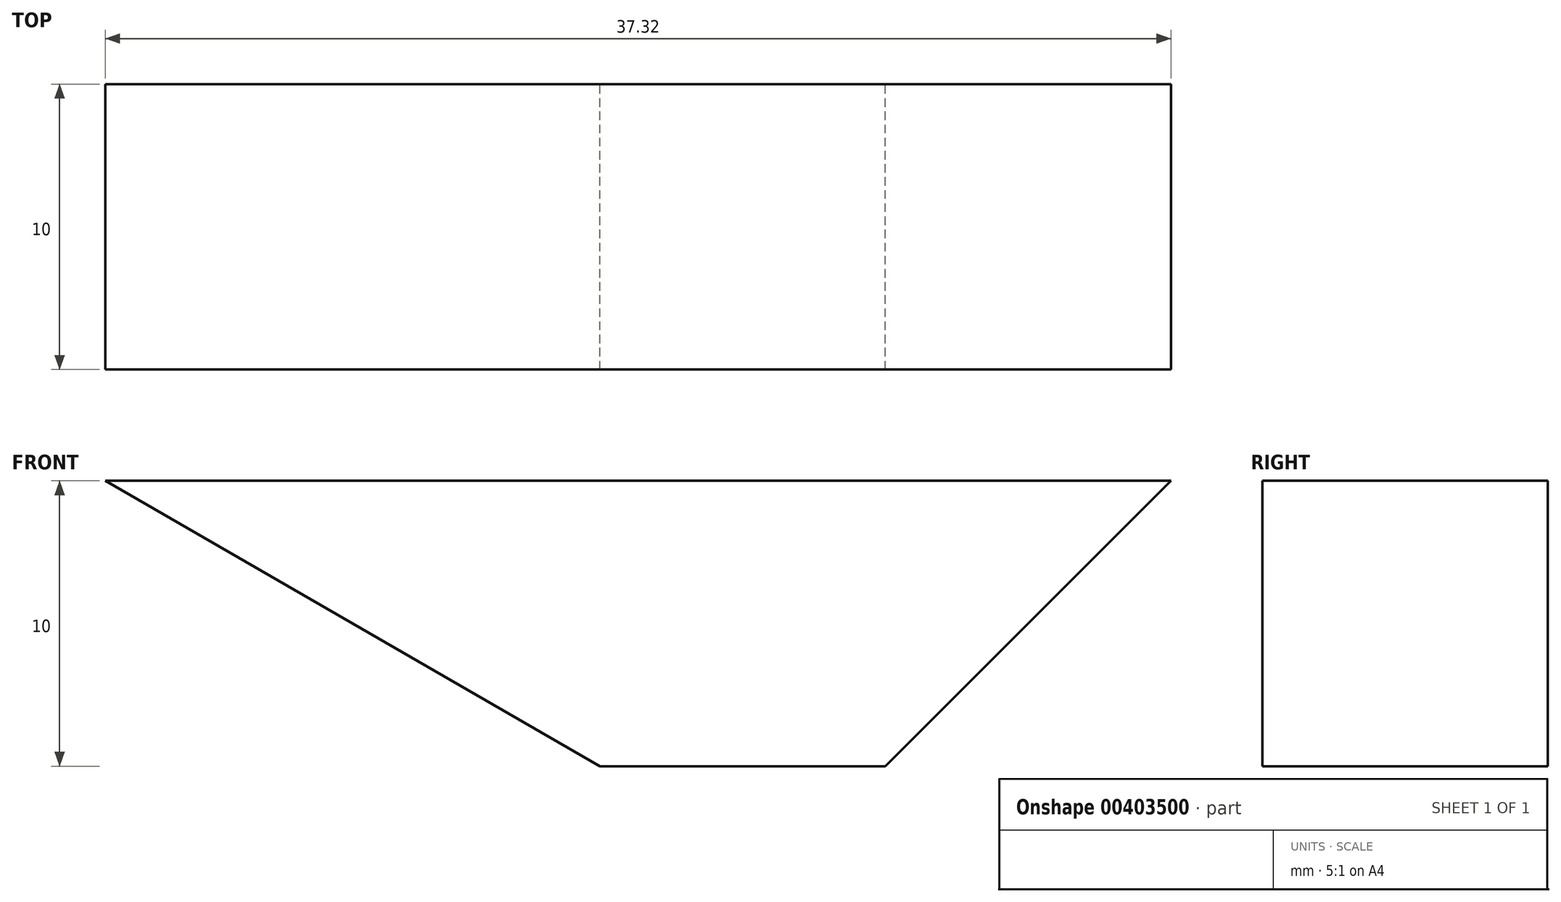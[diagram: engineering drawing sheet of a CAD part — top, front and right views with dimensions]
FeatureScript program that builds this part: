
annotation { "Feature Type Name" : "Feature", "Feature Type Description" : "" }
export const myFeature = defineFeature(function(context is Context, id is Id, definition is map)
    precondition{}
    {
        {
            var Q0;
            Q0=qCreatedBy(makeId("Front.planeOp"),FACE);
            var sketch = newSketch(context, id + "F0", { "sketchPlane" : qUnion([Q0]) });
            skLineSegment(sketch, "E0", {"start": v(0, 0) * mm, "end": v(-17.32, 10) * mm});
            skLineSegment(sketch, "E1", {"start": v(-17.32, 10) * mm, "end": v(20, 10) * mm});
            skLineSegment(sketch, "E2", {"start": v(20, 10) * mm, "end": v(10, 0) * mm});
            skLineSegment(sketch, "E3", {"start": v(10, 0) * mm, "end": v(0, 0) * mm});
            skSolve(sketch);
        }
        {
            var Q0;
            Q0=makeQuery(id+"F0.imprint","IMPRINT",FACE,{"disambiguationData":[TD([[makeQuery(id+"F0.imprint","IMPRINT",EDGE,{"derivedFrom":sQuery(id+"F0.wireOp",EDGE,"E0")}),-1.0]])]});
            extrude(context, id + "F1", {"entities" : qUnion([Q0]), "depth" : 10 * mm});
        }
    });
